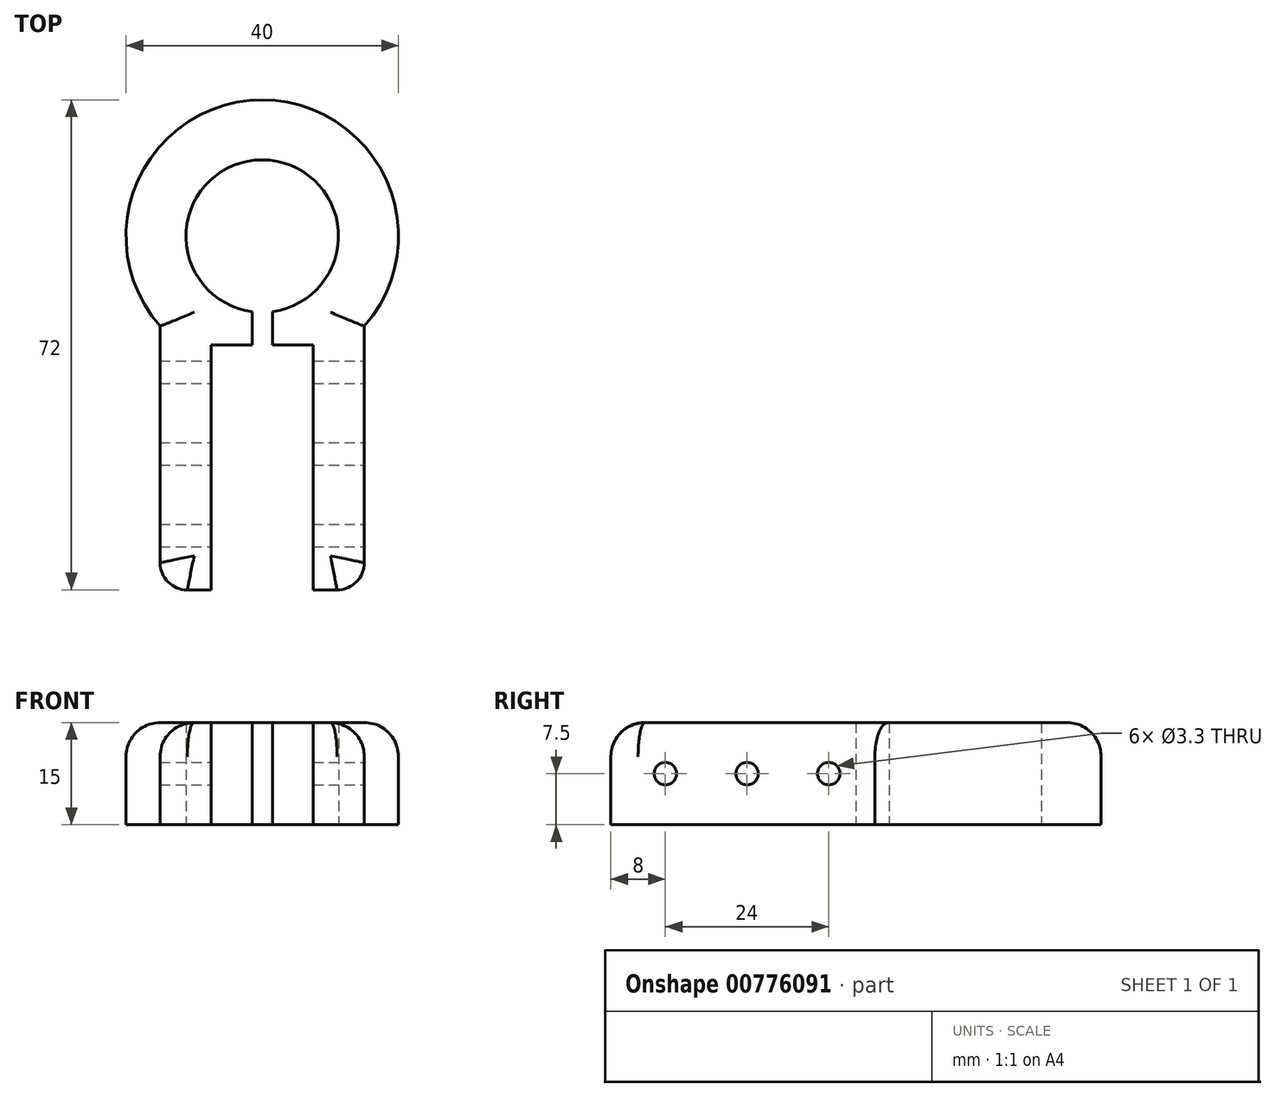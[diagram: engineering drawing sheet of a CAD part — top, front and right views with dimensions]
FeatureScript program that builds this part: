
annotation { "Feature Type Name" : "Feature", "Feature Type Description" : "" }
export const myFeature = defineFeature(function(context is Context, id is Id, definition is map)
    precondition{}
    {
        {
            var Q0;
            Q0=qCreatedBy(makeId("Top.planeOp"),FACE);
            var sketch = newSketch(context, id + "F0", { "sketchPlane" : qUnion([Q0])});
            skLineSegment(sketch, "E0", {"start": v(-1.5, -11.1) * mm, "end": v(-1.5, -16) * mm});
            skLineSegment(sketch, "E1", {"start": v(-1.5, -16) * mm, "end": v(-7.5, -16) * mm});
            skLineSegment(sketch, "E2", {"start": v(-7.5, -16) * mm, "end": v(-7.5, -52) * mm});
            skLineSegment(sketch, "E3", {"start": v(-7.5, -52) * mm, "end": v(-11, -52) * mm});
            skLineSegment(sketch, "E4", {"start": v(-15, -48) * mm, "end": v(-15, -13.23) * mm});
            skLineSegment(sketch, "E5.MirrorCS", {"start": v(1.5, -11.1) * mm, "end": v(1.5, -16) * mm});
            skLineSegment(sketch, "E6.MirrorCS", {"start": v(7.5, -16) * mm, "end": v(7.5, -52) * mm});
            skLineSegment(sketch, "E7.MirrorCS", {"start": v(15, -48) * mm, "end": v(15, -13.23) * mm});
            skLineSegment(sketch, "E8.MirrorCS", {"start": v(1.5, -16) * mm, "end": v(7.5, -16) * mm});
            skLineSegment(sketch, "E9.MirrorCS", {"start": v(7.5, -52) * mm, "end": v(11, -52) * mm});
            skArc(sketch, "E10", {"start": v(-1.5, -11.1) * mm, "mid": v(0, 11.2) * mm, "end": v(1.5, -11.1) * mm});
            skArc(sketch, "E11", {"start": v(-15, -13.23) * mm, "mid": v(0, 20) * mm, "end": v(15, -13.23) * mm});
            skPoint(sketch, "E12.visualSharp", {"position": v(-15, -52) * mm});
            skArc(sketch, "E12.filletArc", {"start": v(-15, -48) * mm, "mid": v(-13.83, -50.83) * mm, "end": v(-11, -52) * mm});
            skPoint(sketch, "E13.visualSharp", {"position": v(15, -52) * mm});
            skArc(sketch, "E13.filletArc", {"start": v(11, -52) * mm, "mid": v(13.83, -50.83) * mm, "end": v(15, -48) * mm});
            skSolve(sketch);
        }
        {
            var Q0;
            Q0=makeQuery(id+"F0.imprint","IMPRINT",FACE,{"disambiguationData":[TD([[makeQuery(id+"F0.imprint","IMPRINT",EDGE,{"derivedFrom":sQuery(id+"F0.wireOp",EDGE,"E0")}),-1.0]])]});
            extrude(context, id + "F1", {"entities" : qUnion([Q0]), "depth" : 7.5 * mm, "offsetDistance" : 25 * mm, "hasSecondDirection" : true, "secondDirectionOppositeDirection" : true, "secondDirectionDepth" : 7.5 * mm});
        }
        {
            var Q0;
            Q0=makeQuery(id+"F1.opExtrude","CAP_EDGE",EDGE,{"disambiguationData":[OSD([sQuery(id+"F0.wireOp",EDGE,"E11")])],"isStart":false});
            var Q1;
            Q1=makeQuery(id+"F1.opExtrude","CAP_EDGE",EDGE,{"disambiguationData":[OSD([sQuery(id+"F0.wireOp",EDGE,"E7.MirrorCS")])],"isStart":false});
            var Q2;
            Q2=makeQuery(id+"F1.opExtrude","CAP_EDGE",EDGE,{"disambiguationData":[OSD([sQuery(id+"F0.wireOp",EDGE,"E4")])],"isStart":false});
            fillet(context, id + "F2", {"entities" : qUnion([Q0, Q1, Q2]), "radius" : 5 * mm, "tangentPropagation" : true, "allowEdgeOverflow" : false});
        }
        {
            var Q0;
            Q0=makeQuery(id+"F1.opExtrude","SWEPT_FACE",FACE,{"disambiguationData":[OSD([sQuery(id+"F0.wireOp",EDGE,"E7.MirrorCS")])]});
            var sketch = newSketch(context, id + "F3", { "sketchPlane" : qUnion([Q0])});
            skLineSegment(sketch, "E14", {"start": v(-44, 0) * mm, "end": v(-20, 0) * mm});
            skPoint(sketch, "E15", {"position": v(-32, 0) * mm});
            skSolve(sketch);
        }
        {
            var Q0;
            Q0=sQuery(id+"F3.wireOp",VERTEX,"E14.start");
            var Q1;
            Q1=sQuery(id+"F3.wireOp",VERTEX,"E15");
            var Q2;
            Q2=sQuery(id+"F3.wireOp",VERTEX,"E14.end");
            var Q3;
            Q3=makeQuery(id+"F1.opExtrude","SWEPT_BODY",BODY,{"disambiguationData":[OSD([sQuery(id+"F0.wireOp",EDGE,"E0"),sQuery(id+"F0.wireOp",EDGE,"E1"),sQuery(id+"F0.wireOp",EDGE,"E2"),sQuery(id+"F0.wireOp",EDGE,"E3"),sQuery(id+"F0.wireOp",EDGE,"E4"),sQuery(id+"F0.wireOp",EDGE,"E5.MirrorCS"),sQuery(id+"F0.wireOp",EDGE,"E6.MirrorCS"),sQuery(id+"F0.wireOp",EDGE,"E7.MirrorCS"),sQuery(id+"F0.wireOp",EDGE,"E8.MirrorCS"),sQuery(id+"F0.wireOp",EDGE,"E9.MirrorCS"),sQuery(id+"F0.wireOp",EDGE,"E10"),sQuery(id+"F0.wireOp",EDGE,"E11"),sQuery(id+"F0.wireOp",EDGE,"E12.filletArc"),sQuery(id+"F0.wireOp",EDGE,"E13.filletArc")])]});
            hole(context, id + "F4", {"style" : HoleStyle.SIMPLE, "endStyle" : HoleEndStyle.BLIND, "standardTappedOrClearance" : lookupTablePath({ "standard" : "ISO", "fit" : "Normal", "size" : "M3", "type" : "Clearance" }), "standardBlindInLast" : lookupTablePath({ "fit" : "Standard", "standard" : "ISO", "size" : "M3", "type" : "Clearance" }), "holeDiameter" : 3.3 * mm, "majorDiameter" : 5 * mm, "holeDepth" : 60 * mm, "isTappedThrough" : true, "tappedDepth" : 12 * mm, "tapClearance" : 3, "locations" : qUnion([Q0, Q1, Q2]), "scope" : qUnion([Q3])});
        }
    });
